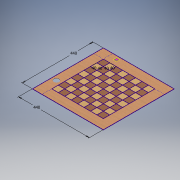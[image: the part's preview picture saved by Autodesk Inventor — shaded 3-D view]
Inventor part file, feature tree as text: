
AUTODESK INVENTOR PART (.ipt)
format: ipt  version: 2019 (Build 230136000, 136)  size: 474,624 bytes
history: native  units: in
note: dims shown in document units (in); Inventor stores cm internally (conversion verified against a paired STEP export)
features: extrude x4, sketch x2, plane x1
ambient origin geometry x8: Origin, YZ Plane, XZ Plane, XY Plane, X Axis, Y Axis, Z Axis, Center Point
bodies: Solid3 (feature_tree), Solid4 (feature_tree)
feature tree (7):
  plane  "Work Plane4"
  sketch  "Sketch2"  dims[d4=1.5748in d5=1.5748in]
  extrude  "Extrusion2"  Depth=1.5748in
  extrude  "Extrusion3"  Depth=17.3228in
  extrude  "Extrusion4"  Depth=17.3228in
  extrude  "Extrusion5"  Depth=0.0787in TaperAngle=0.0deg
  sketch  "Sketch3"  dims[d6=3.1496in d8=1.5748in d9=3.1496in d11=1.5748in d14=17.3228in d15=17.3228in d16=0.0787in d17=0.0in d18=0.0787in d19=0.0in d20=0.0787in d21=0.0in d22=1.2992in d25=0.3937in d26=0.0in d28=4.7244in d29=0.2362in]
